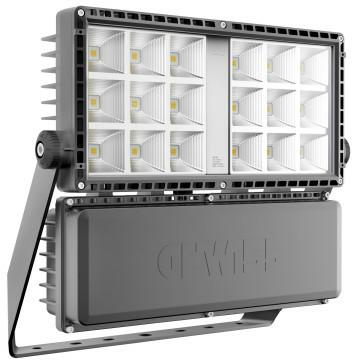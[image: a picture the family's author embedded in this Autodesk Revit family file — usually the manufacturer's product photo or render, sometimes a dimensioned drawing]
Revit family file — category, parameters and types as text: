
# Revit family: Lighting-Proiezione-GEWISS-SMART[PRO]2.0-PROIETTORI-LED-MEDIA-POTENZA_2MODULI_DALI_CLI
name_source: partatom
category: Apparecchi per illuminazione
units: mm (PartAtom-declared; Revit-internal decimal feet)

## family parameters
Condiviso = No
Host = Superficie
Punto di calcolo locali = No
Quota connettore circolare = Usa diametro
Sorgente d'illuminazione = No
Taglio con vuoti quando caricato = No
Tipo di parte = Normale

## types (1)
- Lighting-Proiezione-GEWISS-SMART[PRO]2.0-PROIETTORI-LED-MEDIA-POTENZA_2MODULI_DALI_CLI
    Alimentatore = Incluso
    Apparecchio a ridotta temperatura superficiale = No
    Applicazione = Interno / Esterno
    Cablaggio = Connettore stagno
    Caratteristiche elettriche e gestione della luce = -
    Caratteristiche ottiche e illuminotecniche = -
    Catalogo = LIGHTING
    Certificazione DIN 18032-3 = Si
    Certificazioni e classificazioni = -
    Classe fotobiologica = -
    Classe isolamento = I
    Classificazione: = -
    Codice digitale univoco (Datamatrix) = Attualmente non presente
    Colore = Grigio grafite
    Contesto = Illuminazione di grandi aree, impianti sportivi
    Controllo abbagliamento e luminanza = G*6 - ULOR = 0
    Corpo = Alluminio pressofuso
    Descrizione = SMARTPRO2.0 2M 5700K CRI80 A3 DALI CL1
    Dispositivo di protezione = DM 6 kV / CM 10 kV
    Durata di vita = L90B10 (Tq+25°C) - 40000h L90B10 (Tq+50°C) = 32000h L80B10 (Tq+25°C) - 90000h
    Efficienza luminosa (lm/W) = 113
    Finitura colore = Verniciato a polvere poliestere
    Fissaggio = Staffa
    Frequenza nominale (Hz) = 50 / 60
    GW - Codice Electrocod = 2424
    Gancio di chiusura = Viti metriche esagonali
    Garanzia = 5 anni
    Grado di protezione = IP66
    Gruppo ottico = Parabola in alluminio anodizzato brillantato con alluminio puro 99,99%
    Guarnizioni = silicone antinvecchiamento
    IDF = 2baeb83e-fb93-4ee6-8b3b-a462765b39a8
    IDT = 256691c01990452284852cf61e57a00c
    IPEA = STRADALE = A // GRANDI AREE = A3+ // CICLOPEDONALI = A+ // AREE VERDI = A+ // CENTRO STORICO = A5+ // ALTRO = A5+
    Immagine tipo = GWP2274AD.jpg
    Inclinazione = Rotazione su staffa con goniometro integrato
    Indice di resa cromatica = CRI-80
    Informazioni generali = -
    Installazione e manutenzione = -
    Lampada = LED
    Lumen output (lm) = 37200
    Materiali = -
    Modello = GWP2285ND
    Norma di riferimento = EN60598-1; EN60598-2-5; IEC 62778; IEC 62471; EN13201
    Ottica = A3 - Asimmetrica Stretta
    Peso (kg): = 13
    Potenza di sistema = 330W
    Produttore = GEWISS S.p.A.
    Prospetto di default = 1219 mm
    Resistenza agli urti = IK08
    Resistenza al filo incandescente = -
    SEO = Proiettore
    Scheda Tecnica = https://www.gewiss.com
    Schermo = Vetro piano extrachiaro spessore 4mm
    Sistema di controllo = DALI
    Sostituibilità gruppo ottico = Non disponibile
    Sostituibilità piastra di cablaggio = Non disponibile
    Spostamento_x = 2186 mm
    Spostamento_x_effettivo = 1814 mm
    Superficie massima esposta al vento : = 0,170 m2
    Temperatura di colore = 5700K
    Temperatura di esercizio = -30 +50 °C
    Temperatura di stoccaggio = -
    Tensione di alimentazione = 220 - 240 V
    Tipo di apparecchio = Apparecchio per proiezione LED di piccola, media e alta potenza
    Tipo di installazione e montaggio = Torrefaro - Parete - Terra
    Tipologia sorgente luminosa = LED - Non sostituibile
    Tolleranza cromatica = SDCM = 3
    URL = https://www.gewiss.com
    Vano di alimentazione = Integrato
    Versione file RFA = 20.11
    Versioni = Luce fredda 5700K
    Viti esterne = Acciaio inossidabile
